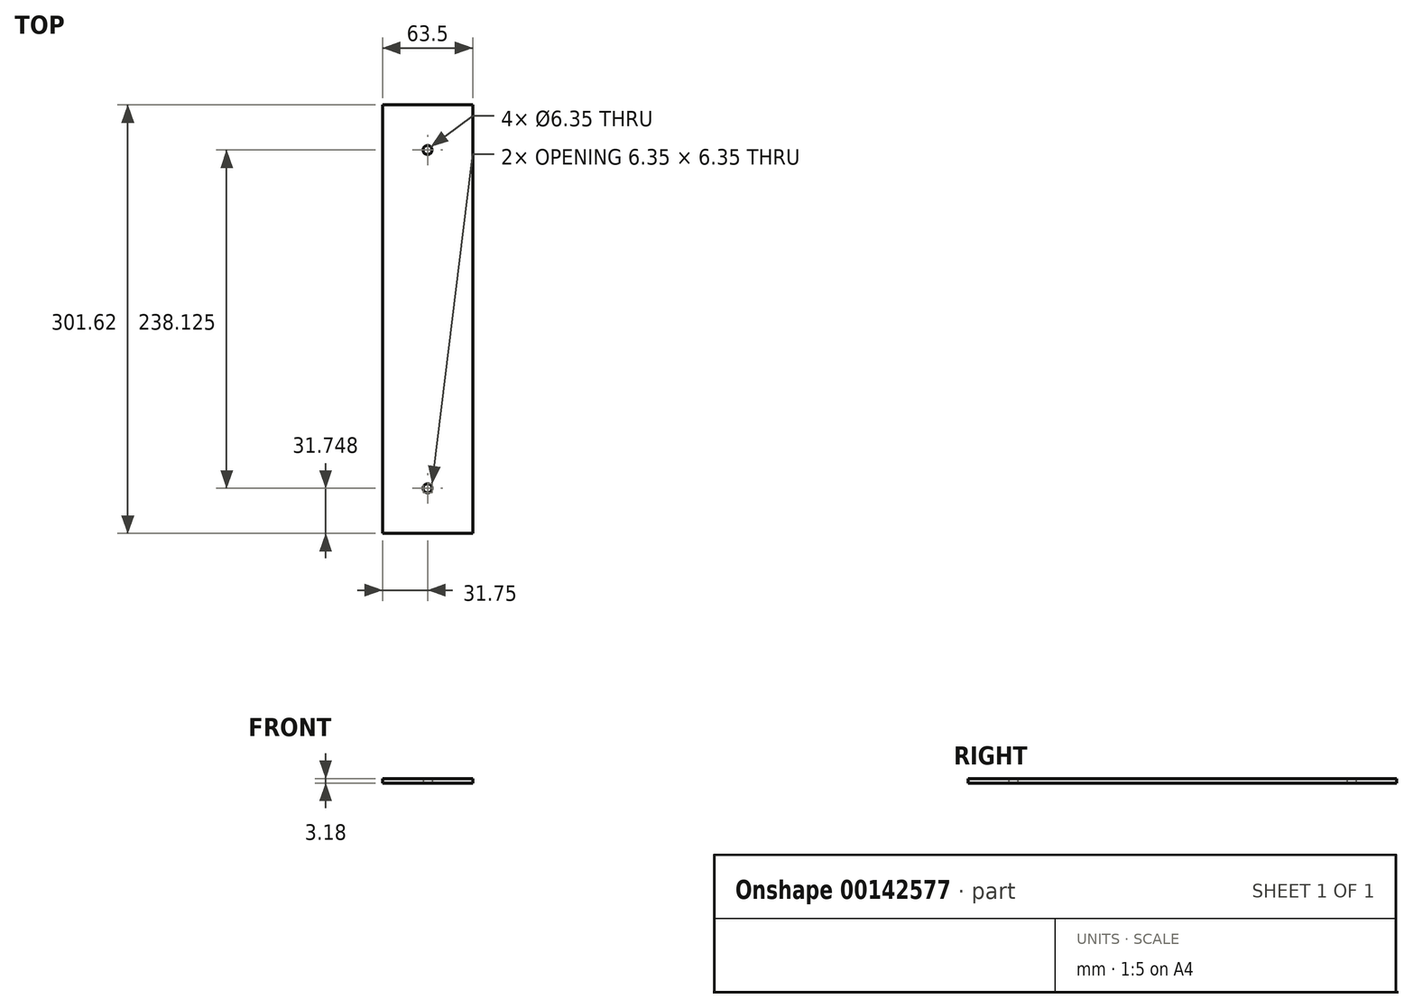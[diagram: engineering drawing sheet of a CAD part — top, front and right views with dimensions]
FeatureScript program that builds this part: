
annotation { "Feature Type Name" : "Feature", "Feature Type Description" : "" }
export const myFeature = defineFeature(function(context is Context, id is Id, definition is map)
    precondition{}
    {
        {
            var Q0;
            Q0=qCreatedBy(makeId("Top.planeOp"),FACE);
            var sketch = newSketch(context, id + "F0", { "sketchPlane" : qUnion([Q0])});
            skLineSegment(sketch, "E0.bottom", {"start": v(31.75, 150.81) * mm, "end": v(-31.75, 150.81) * mm});
            skLineSegment(sketch, "E0.top", {"start": v(31.75, -150.81) * mm, "end": v(-31.75, -150.81) * mm});
            skLineSegment(sketch, "E0.left", {"start": v(31.75, 150.81) * mm, "end": v(31.75, -150.81) * mm});
            skLineSegment(sketch, "E0.right", {"start": v(-31.75, 150.81) * mm, "end": v(-31.75, -150.81) * mm});
            skPoint(sketch, "E0.middle", {"position": v(0, 0) * mm});
            skPoint(sketch, "E1", {"position": v(0, -119.06) * mm});
            skPoint(sketch, "E2", {"position": v(0, 119.06) * mm});
            skLineSegment(sketch, "E3", {"start": v(-31.75, -119.06) * mm, "end": v(31.75, -119.06) * mm});
            skLineSegment(sketch, "E4", {"start": v(0, -119.06) * mm, "end": v(0, 119.06) * mm});
            skLineSegment(sketch, "E5", {"start": v(0, 119.06) * mm, "end": v(0, 150.81) * mm});
            skLineSegment(sketch, "E6", {"start": v(0, -119.06) * mm, "end": v(0, -150.81) * mm});
            skSolve(sketch);
        }
        {
            var Q0;
            Q0=makeQuery(id+"F0.imprint","IMPRINT",FACE,{"disambiguationData":[TD([[makeQuery(id+"F0.imprint","IMPRINT",EDGE,{"derivedFrom":sQuery(id+"F0.wireOp",EDGE,"E0.bottom")}),1.0]])]});
            var Q1;
            {var subQ0=sQuery(id+"F0.wireOp",EDGE,"ObzlJ2qy-F3cb-5kpE-wg9l-YNl24hn9BEZk");Q1=makeQuery(id+"F0.imprint","IMPRINT",FACE,{"disambiguationData":[TD([[makeQuery(id+"F0.imprint","IMPRINT",EDGE,{"derivedFrom":subQ0}),-1.0]])]});}
            var Q2;
            {var subQ0=sQuery(id+"F0.wireOp",EDGE,"E0.top");Q2=makeQuery(id+"F0.imprint","IMPRINT",FACE,{"disambiguationData":[TD([[makeQuery(id+"F0.imprint","IMPRINT",EDGE,{"derivedFrom":subQ0}),-1.0]])]});}
            extrude(context, id + "F1", {"entities" : qUnion([Q0, Q1, Q2]), "offsetDistance" : 25.4 * mm, "depth" : 3.17 * mm});
        }
        {
            var Q0;
            Q0 = qSketchRegion(id + "F0", true);
            extrude(context, id + "F2", {"entities" : qUnion([Q0]), "depth" : 3.17 * mm});
        }
        {
            var Q0;
            Q0=sQuery(id+"F0.wireOp",VERTEX,"E1");
            var Q1;
            Q1=sQuery(id+"F0.wireOp",VERTEX,"E2");
            var Q2;
            Q2=makeQuery(id+"F2.opExtrude","SWEPT_BODY",BODY,{"disambiguationData":[OSD([sQuery(id+"F0.wireOp",EDGE,"E0.bottom"),sQuery(id+"F0.wireOp",EDGE,"E0.top"),sQuery(id+"F0.wireOp",EDGE,"E0.left"),sQuery(id+"F0.wireOp",EDGE,"E0.right")])]});
            var Q3;
            Q3=makeQuery(id+"F1.opExtrude","SWEPT_BODY",BODY,{"disambiguationData":[OSD([sQuery(id+"F0.wireOp",EDGE,"E0.bottom"),sQuery(id+"F0.wireOp",EDGE,"E0.top"),sQuery(id+"F0.wireOp",EDGE,"E0.left"),sQuery(id+"F0.wireOp",EDGE,"E0.right")])]});
            hole(context, id + "F3", {"style" : HoleStyle.SIMPLE, "endStyle" : HoleEndStyle.THROUGH, "oppositeDirection" : true, "holeDiameter" : 6.35 * mm, "locations" : qUnion([Q0, Q1]), "scope" : qUnion([Q2, Q3]), "isTappedThrough" : true});
        }
    });
